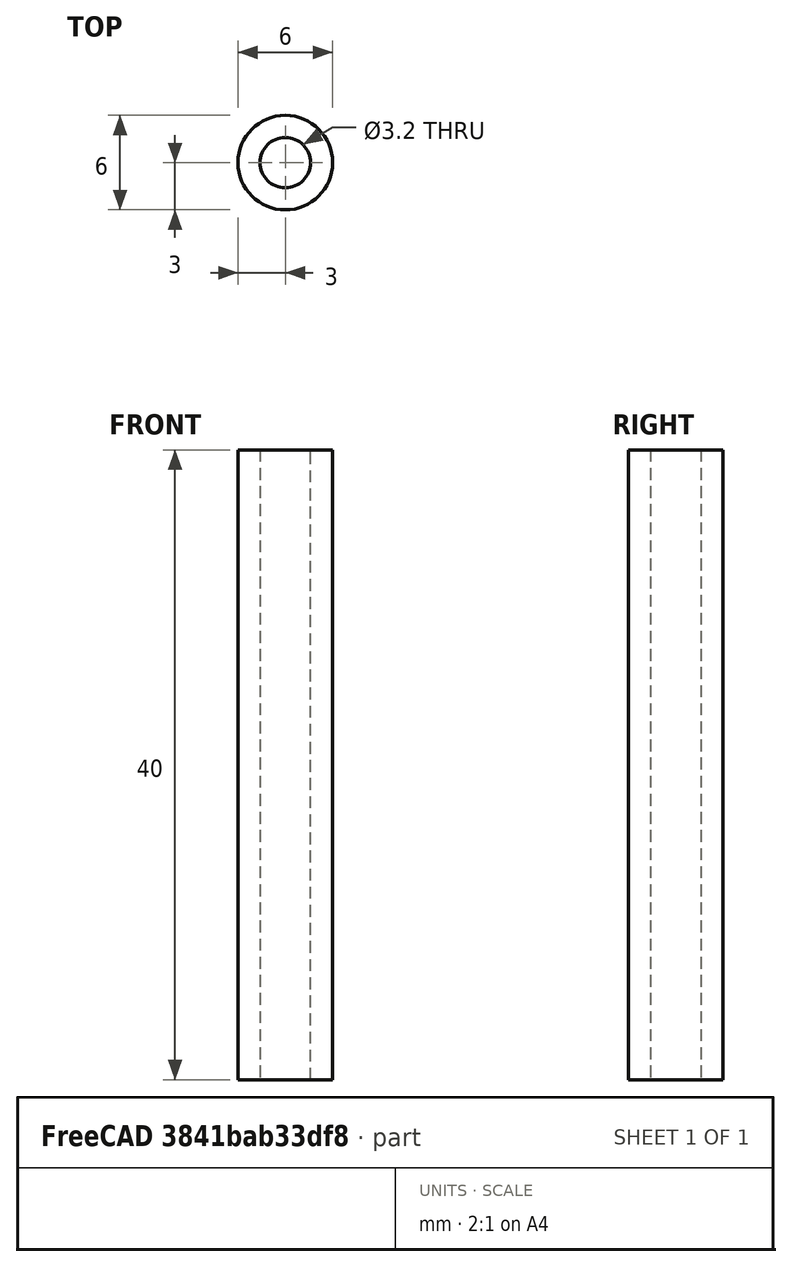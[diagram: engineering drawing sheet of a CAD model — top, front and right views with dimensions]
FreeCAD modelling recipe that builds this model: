
FCSTD DOCUMENT  (FreeCAD 1.0R39109 (Git))
Label: 40mm_spacer
License: All rights reserved
LicenseURL: https://en.wikipedia.org/wiki/All_rights_reserved
objects: Sketcher::SketchObject×1, PartDesign::Pad×1, PartDesign::Body×1
note: 6 computed .brp shape members not serialized (recipe doc carries the construction recipe); baked Part::Feature solids carry a one-line shape summary decoded from their .brp

FEATURE [Sketcher::SketchObject] Sketch
  ArcFitTolerance = 1e-06
  AttachmentSupport = -> [XY_Plane]
  FullyConstrained = true
  MakeInternals = false
  MapMode = 5
  sketch-geometry (2):
    g0: Circle CenterX=0 CenterY=0 CenterZ=0 NormalX=0 NormalY=0 NormalZ=1 AngleXU=0 Radius=1.6
    g1: Circle CenterX=0 CenterY=0 CenterZ=0 NormalX=0 NormalY=0 NormalZ=1 AngleXU=0 Radius=3
  constraints (4):
    c: Coincident(g0,g-1)
    c: Coincident(g1,g0)
    c: Diameter(g0) = 3.2
    c: Diameter(g1) = 6
FEATURE [PartDesign::Pad] Pad
  Direction = (0,0,1)
  Length = 40
  Length2 = 10
  Profile = -> Sketch
  ReferenceAxis = -> Sketch [N_Axis]
  Refine = true
  Suppressed = false
  Type = 0
FEATURE [PartDesign::Body] Body
  AllowCompound = false
  Group = -> [Sketch,Pad]
  Origin = -> Origin
  Tip = -> Pad
